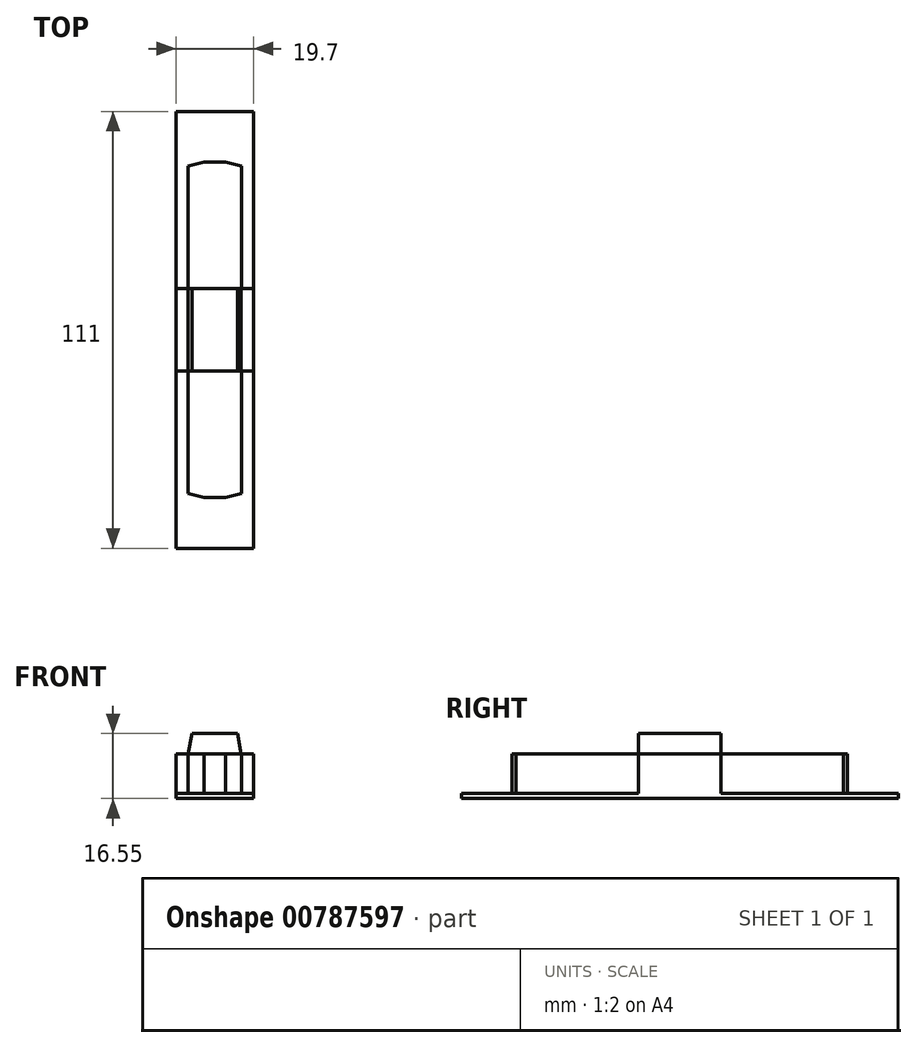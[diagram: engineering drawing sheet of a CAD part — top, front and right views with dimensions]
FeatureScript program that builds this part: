
annotation { "Feature Type Name" : "Feature", "Feature Type Description" : "" }
export const myFeature = defineFeature(function(context is Context, id is Id, definition is map)
    precondition{}
    {
        {
            var Q0;
            Q0=qCreatedBy(makeId("Top.planeOp"),FACE);
            var sketch = newSketch(context, id + "F0", { "sketchPlane" : qUnion([Q0])});
            skLineSegment(sketch, "E0.bottom", {"start": v(0, 0) * mm, "end": v(19.7, 0) * mm});
            skLineSegment(sketch, "E0.top", {"start": v(0, 111) * mm, "end": v(19.7, 111) * mm});
            skLineSegment(sketch, "E0.left", {"start": v(0, 0) * mm, "end": v(0, 111) * mm});
            skLineSegment(sketch, "E0.right", {"start": v(19.7, 0) * mm, "end": v(19.7, 111) * mm});
            skSolve(sketch);
        }
        {
            var Q0;
            Q0 = qSketchRegion(id + "F0", true);
            extrude(context, id + "F1", {"entities" : qUnion([Q0]), "depth" : 1.3 * mm, "offsetDistance" : 25 * mm});
        }
        {
            var Q0;
            Q0=makeQuery(id+"F1.opExtrude","CAP_FACE",FACE,{"disambiguationData":[OSD([sQuery(id+"F0.wireOp",EDGE,"E0.bottom"),sQuery(id+"F0.wireOp",EDGE,"E0.top"),sQuery(id+"F0.wireOp",EDGE,"E0.left"),sQuery(id+"F0.wireOp",EDGE,"E0.right")])],"isStart":false});
            var sketch = newSketch(context, id + "F2", { "sketchPlane" : qUnion([Q0])});
            skLineSegment(sketch, "E1.bottom", {"start": v(7.07, 98.1) * mm, "end": v(12.62, 98.1) * mm});
            skLineSegment(sketch, "E1.top", {"start": v(3.08, 12.9) * mm, "end": v(3.08, 12.9) * mm});
            skLineSegment(sketch, "E1.left", {"start": v(3.07, 97.1) * mm, "end": v(3.08, 13.9) * mm});
            skLineSegment(sketch, "E1.right", {"start": v(16.62, 97.1) * mm, "end": v(16.63, 13.9) * mm});
            skLineSegment(sketch, "E2", {"start": v(7.08, 12.9) * mm, "end": v(3.07, 13.9) * mm});
            skLineSegment(sketch, "E3", {"start": v(7.08, 12.9) * mm, "end": v(12.62, 12.9) * mm});
            skLineSegment(sketch, "E4", {"start": v(12.62, 12.9) * mm, "end": v(16.63, 13.9) * mm});
            skLineSegment(sketch, "E5", {"start": v(3.07, 97.1) * mm, "end": v(7.07, 98.1) * mm});
            skLineSegment(sketch, "E6", {"start": v(12.62, 98.1) * mm, "end": v(16.62, 97.1) * mm});
            skSolve(sketch);
        }
        {
            var Q0;
            Q0 = qSketchRegion(id + "F2", true);
            extrude(context, id + "F3", {"entities" : qUnion([Q0]), "operationType" : NewBodyOperationType.ADD, "depth" : 10 * mm, "offsetDistance" : 25 * mm});
        }
        {
            var Q0;
            Q0=makeQuery(id+"F1.opExtrude","CAP_FACE",FACE,{"disambiguationData":[OSD([sQuery(id+"F0.wireOp",EDGE,"E0.bottom"),sQuery(id+"F0.wireOp",EDGE,"E0.top"),sQuery(id+"F0.wireOp",EDGE,"E0.left"),sQuery(id+"F0.wireOp",EDGE,"E0.right")])],"isStart":false});
            var sketch = newSketch(context, id + "F4", { "sketchPlane" : qUnion([Q0])});
            skLineSegment(sketch, "E7.bottom", {"start": v(0, 45) * mm, "end": v(19.7, 45) * mm});
            skLineSegment(sketch, "E7.top", {"start": v(0, 66) * mm, "end": v(19.7, 66) * mm});
            skLineSegment(sketch, "E7.left", {"start": v(0, 45) * mm, "end": v(0, 66) * mm});
            skLineSegment(sketch, "E7.right", {"start": v(19.7, 45) * mm, "end": v(19.7, 66) * mm});
            skSolve(sketch);
        }
        {
            var Q0;
            Q0 = qSketchRegion(id + "F4", true);
            extrude(context, id + "F5", {"entities" : qUnion([Q0]), "operationType" : NewBodyOperationType.ADD, "depth" : 10 * mm, "offsetDistance" : 25 * mm});
        }
        {
            var Q0;
            {var subQ1=sQuery(id+"F0.wireOp",EDGE,"E0.left");var subQ3=sQuery(id+"F4.wireOp",EDGE,"E7.top");Q0=makeQuery(id+"F5.boolean.opBoolean","SPLIT",FACE,{"disambiguationData":[TD([makeQuery(id+"F1.opExtrude","SWEPT_FACE",FACE,{"disambiguationData":[OSD([subQ1])]})])],"derivedFrom":makeQuery(id+"F5.opExtrude","SWEPT_FACE",FACE,{"disambiguationData":[OSD([subQ3])]})});}
            var sketch = newSketch(context, id + "F6", { "sketchPlane" : qUnion([Q0])});
            skLineSegment(sketch, "E8", {"start": v(-3.07, 11.3) * mm, "end": v(-4.13, 16.55) * mm});
            skLineSegment(sketch, "E9", {"start": v(-4.13, 16.55) * mm, "end": v(-15.63, 16.55) * mm});
            skLineSegment(sketch, "E10", {"start": v(-15.63, 16.55) * mm, "end": v(-16.58, 11.3) * mm});
            skLineSegment(sketch, "E11", {"start": v(-3.07, 11.3) * mm, "end": v(-16.57, 11.3) * mm});
            skSolve(sketch);
        }
        {
            var Q0;
            Q0 = qSketchRegion(id + "F6", true);
            var Q1;
            {var subQ1=sQuery(id+"F0.wireOp",EDGE,"E0.left");var subQ3=sQuery(id+"F4.wireOp",EDGE,"E7.bottom");Q1=makeQuery(id+"F5.boolean.opBoolean","SPLIT",FACE,{"disambiguationData":[TD([makeQuery(id+"F1.opExtrude","SWEPT_FACE",FACE,{"disambiguationData":[OSD([subQ1])]})])],"derivedFrom":makeQuery(id+"F5.opExtrude","SWEPT_FACE",FACE,{"disambiguationData":[OSD([subQ3])]})});}
            extrude(context, id + "F7", {"entities" : qUnion([Q0]), "operationType" : NewBodyOperationType.ADD, "endBound" : BoundingType.UP_TO_SURFACE, "oppositeDirection" : true, "depth" : 21 * mm, "endBoundEntityFace" : qUnion([Q1]), "offsetDistance" : 25 * mm});
        }
    });
